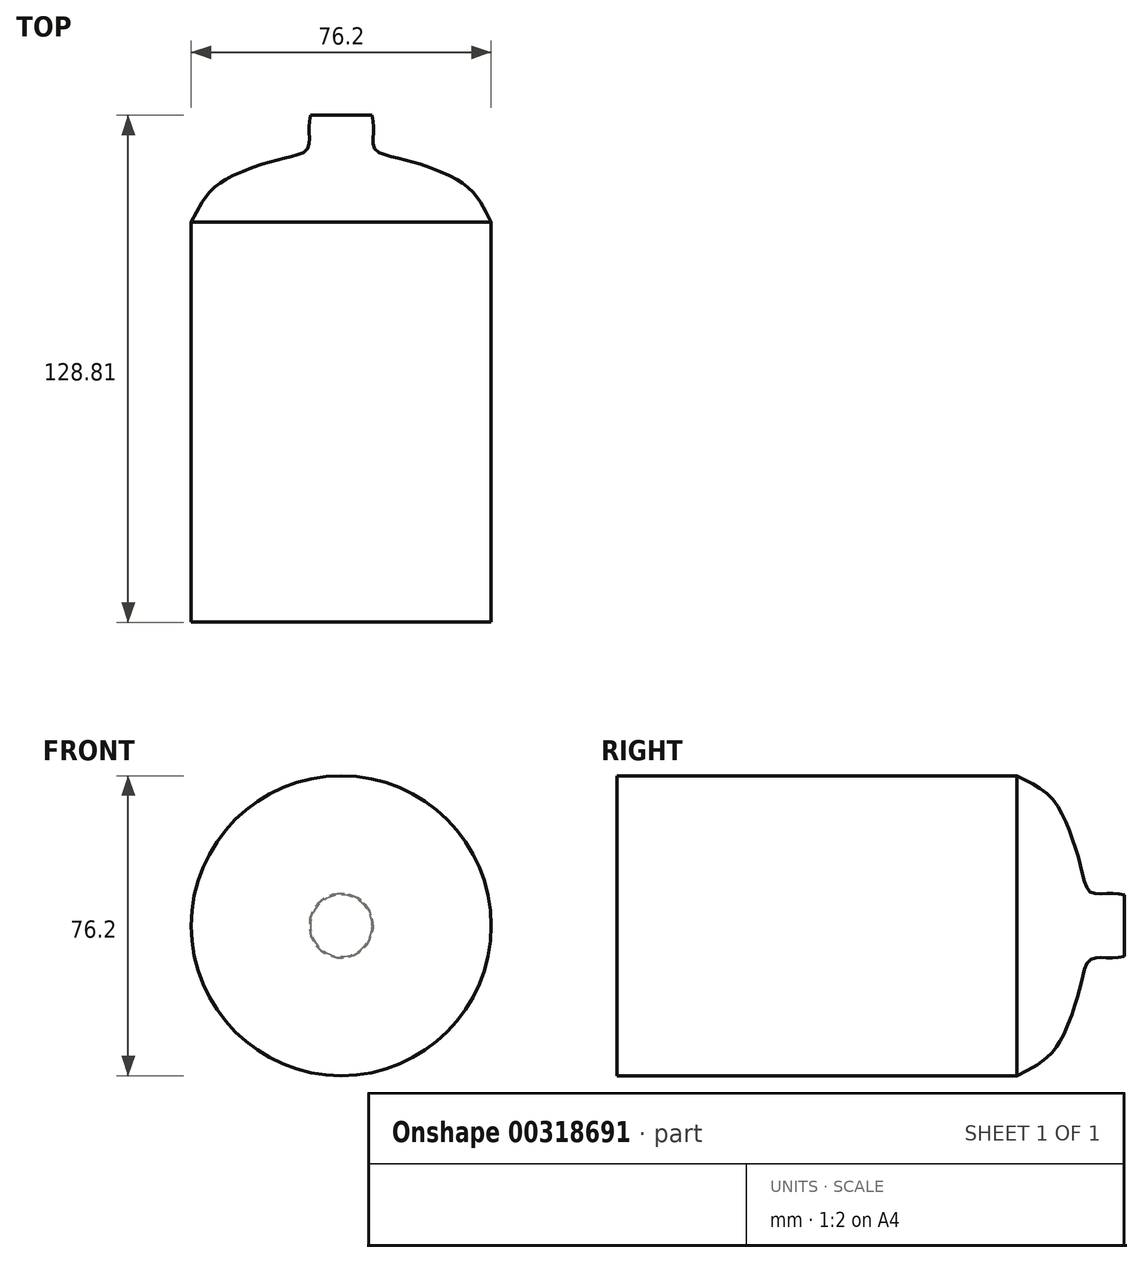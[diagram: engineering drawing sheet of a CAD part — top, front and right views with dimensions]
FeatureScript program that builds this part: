
annotation { "Feature Type Name" : "Feature", "Feature Type Description" : "" }
export const myFeature = defineFeature(function(context is Context, id is Id, definition is map)
    precondition{}
    {
        {
            var Q0;
            Q0=qCreatedBy(makeId("Top.planeOp"),FACE);
            var sketch = newSketch(context, id + "F0", { "sketchPlane" : qUnion([Q0])});
            skLineSegment(sketch, "E0", {"start": v(-38.1, 39.53) * mm, "end": v(-38.1, -62.07) * mm});
            skLineSegment(sketch, "E1", {"start": v(-38.1, -62.07) * mm, "end": v(0, -62.07) * mm});
            skPoint(sketch, "E2.1.internal.orphan", {"position": v(-38.1, 47.78) * mm});
            skFitSpline(sketch, "E3", {"points": [v(-38.1, 39.53) * mm, v(-32.9, 47.78) * mm, v(-24.3, 52.79) * mm, v(-13.92, 56) * mm, v(-8.56, 58.15) * mm, v(-8.2, 62.45) * mm, v(-7.84, 66.74) * mm], "startDerivative": vector(22.96, 46.56) * mm, "endDerivative": vector(4.73, 32.12) * mm});
            skLineSegment(sketch, "E4", {"start": v(-7.84, 66.74) * mm, "end": v(0, 66.74) * mm});
            skLineSegment(sketch, "E5", {"start": v(0, 66.74) * mm, "end": v(0, -62.07) * mm});
            skSolve(sketch);
        }
        {
            var Q0;
            Q0=qCreatedBy(makeId("Top.planeOp"),FACE);
            var sketch = newSketch(context, id + "F1", { "sketchPlane" : qUnion([Q0])});
            skLineSegment(sketch, "E6", {"start": v(0, 73.08) * mm, "end": v(0, -71.65) * mm, "construction": true});
            skSolve(sketch);
        }
        {
            var Q0;
            Q0=makeQuery(id+"F0.imprint","IMPRINT",FACE,{"disambiguationData":[TD([[makeQuery(id+"F0.imprint","IMPRINT",EDGE,{"derivedFrom":sQuery(id+"F0.wireOp",EDGE,"E0")}),1.0]])]});
            var Q1;
            Q1=sQuery(id+"F1.wireOp",EDGE,"E6");
            revolve(context, id + "F2", {"entities" : qUnion([Q0]), "axis" : qUnion([Q1]), "revolveType" : RevolveType.FULL});
        }
    });
